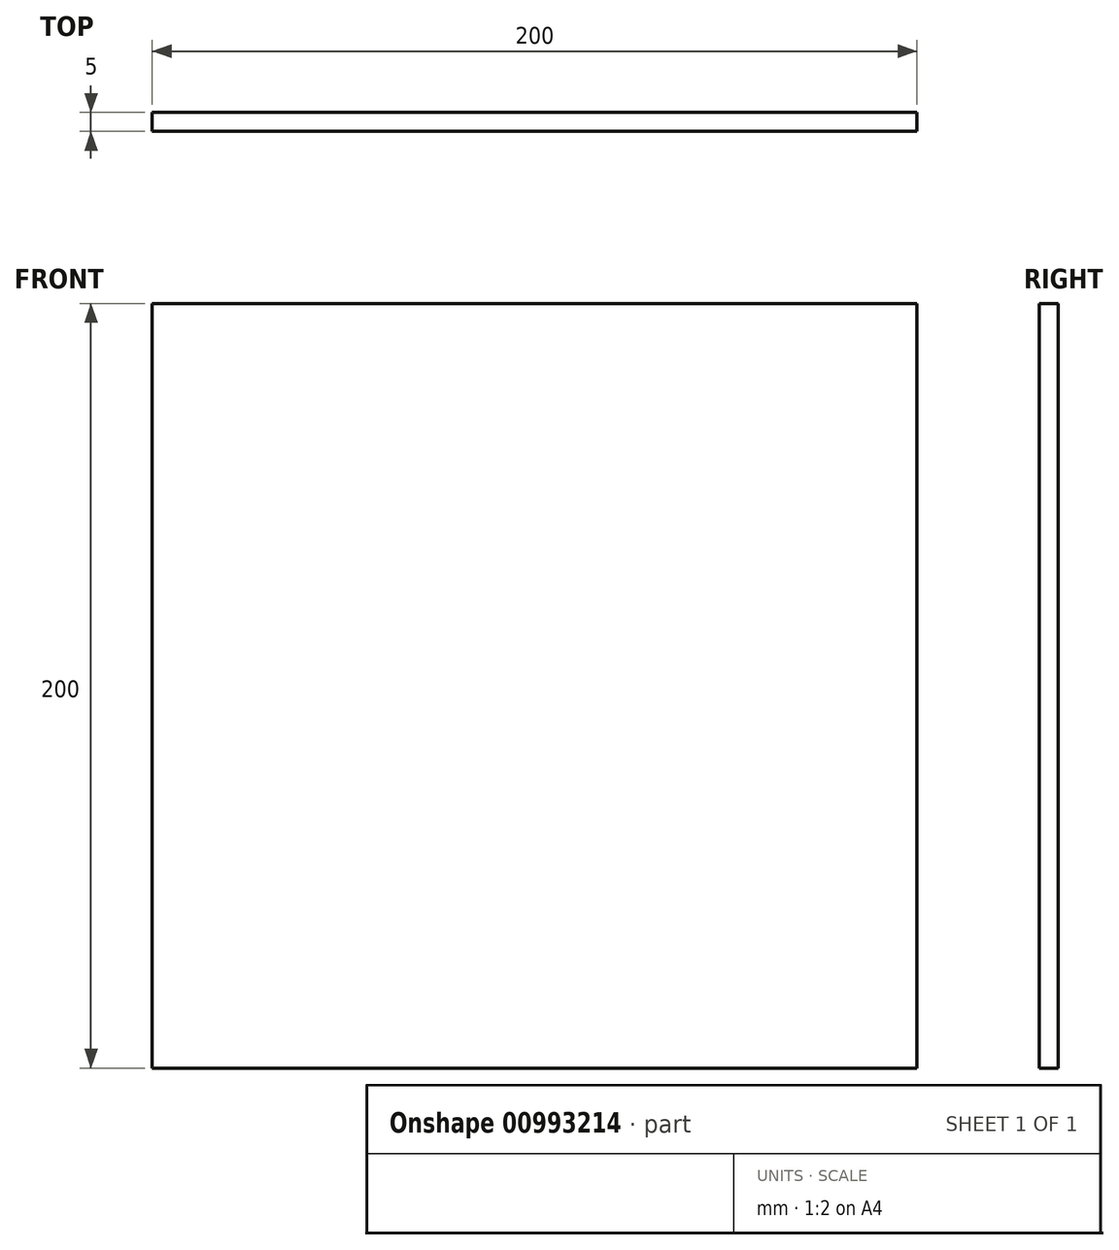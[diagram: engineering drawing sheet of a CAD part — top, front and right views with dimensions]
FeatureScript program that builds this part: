
annotation { "Feature Type Name" : "Feature", "Feature Type Description" : "" }
export const myFeature = defineFeature(function(context is Context, id is Id, definition is map)
    precondition{}
    {
        {
            var Q0;
            Q0=qCreatedBy(makeId("Front.planeOp"),FACE);
            var sketch = newSketch(context, id + "F0", { "sketchPlane" : qUnion([Q0])});
            skLineSegment(sketch, "E0.bottom", {"start": v(-103.95, 125.22) * mm, "end": v(96.05, 125.22) * mm});
            skLineSegment(sketch, "E0.top", {"start": v(-103.95, -74.78) * mm, "end": v(96.05, -74.78) * mm});
            skLineSegment(sketch, "E0.left", {"start": v(-103.95, 125.22) * mm, "end": v(-103.95, -74.78) * mm});
            skLineSegment(sketch, "E0.right", {"start": v(96.05, 125.22) * mm, "end": v(96.05, -74.78) * mm});
            skSolve(sketch);
        }
        {
            var Q0;
            Q0 = qSketchRegion(id + "F0", true);
            extrude(context, id + "F1", {"entities" : qUnion([Q0]), "depth" : 5 * mm, "offsetDistance" : 25 * mm});
        }
    });
